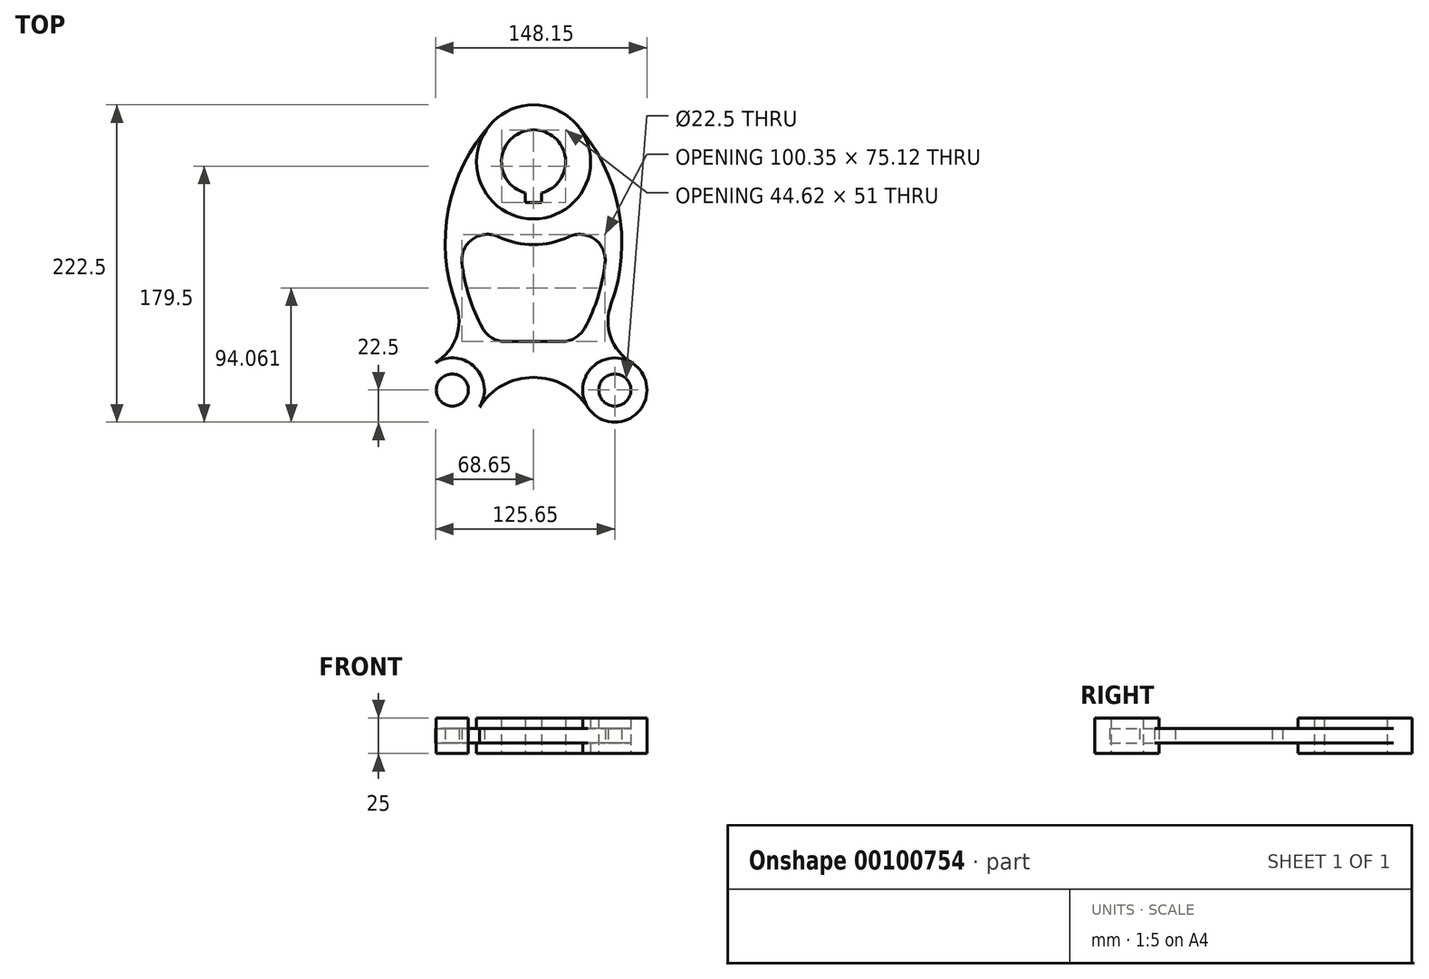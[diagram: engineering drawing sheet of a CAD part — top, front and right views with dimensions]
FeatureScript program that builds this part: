
annotation { "Feature Type Name" : "Feature", "Feature Type Description" : "" }
export const myFeature = defineFeature(function(context is Context, id is Id, definition is map)
    precondition{}
    {
        {
            var Q0;
            Q0=qCreatedBy(makeId("Top.planeOp"),FACE);
            var sketch = newSketch(context, id + "F0", { "sketchPlane" : qUnion([Q0])});
            skArc(sketch, "E0", {"start": v(5.75, -21.75) * mm, "mid": v(0, 22.5) * mm, "end": v(-5.75, -21.75) * mm});
            skCircle(sketch, "E1", {"center": v(0, 0) * mm, "radius": 40 * mm});
            skCircle(sketch, "E2", {"center": v(57, -160) * mm, "radius": 11.25 * mm});
            skCircle(sketch, "E3", {"center": v(57, -160) * mm, "radius": 22.5 * mm});
            skLineSegment(sketch, "E4", {"start": v(-5.75, -28.5) * mm, "end": v(5.75, -28.5) * mm});
            skLineSegment(sketch, "E5", {"start": v(-5.75, -28.5) * mm, "end": v(-5.75, -21.75) * mm});
            skLineSegment(sketch, "E6", {"start": v(5.75, -28.5) * mm, "end": v(5.75, -21.75) * mm});
            skLineSegment(sketch, "E7", {"start": v(0, -126) * mm, "end": v(20, -126) * mm});
            skArc(sketch, "E8", {"start": v(0, -58) * mm, "mid": v(12.62, -56.61) * mm, "end": v(24.64, -52.5) * mm});
            skArc(sketch, "E9", {"start": v(50.17, -70.79) * mm, "mid": v(42.76, -54.17) * mm, "end": v(24.64, -52.5) * mm});
            skArc(sketch, "E10", {"start": v(54.33, -99.97) * mm, "mid": v(59.65, -33.14) * mm, "end": v(29.67, 26.82) * mm});
            skLineSegment(sketch, "E11", {"start": v(0, 60.43) * mm, "end": v(0, -244.32) * mm, "construction": true});
            skArc(sketch, "E12", {"start": v(54.33, -99.97) * mm, "mid": v(54.17, -122.93) * mm, "end": v(68.65, -140.75) * mm});
            skArc(sketch, "E13", {"start": v(20, -126) * mm, "mid": v(29.2, -123.47) * mm, "end": v(35.82, -116.58) * mm});
            skArc(sketch, "E14.trimOffspring", {"start": v(35.82, -116.58) * mm, "mid": v(45.22, -94.38) * mm, "end": v(50.17, -70.79) * mm});
            skArc(sketch, "E15.MirrorCS", {"start": v(-35.82, -116.58) * mm, "mid": v(-45.22, -94.38) * mm, "end": v(-50.17, -70.79) * mm});
            skArc(sketch, "E16.MirrorCS", {"start": v(-54.33, -99.97) * mm, "mid": v(-59.65, -33.14) * mm, "end": v(-29.67, 26.82) * mm});
            skCircle(sketch, "E17.MirrorC", {"center": v(-57, -160) * mm, "radius": 22.5 * mm});
            skArc(sketch, "E18.MirrorCS", {"start": v(-54.33, -99.97) * mm, "mid": v(-54.17, -122.93) * mm, "end": v(-68.65, -140.75) * mm});
            skArc(sketch, "E19.MirrorCS", {"start": v(-20, -126) * mm, "mid": v(-29.2, -123.47) * mm, "end": v(-35.82, -116.58) * mm});
            skCircle(sketch, "E20.MirrorC", {"center": v(-57, -160) * mm, "radius": 11.25 * mm});
            skArc(sketch, "E21.MirrorCS", {"start": v(-50.17, -70.79) * mm, "mid": v(-42.76, -54.17) * mm, "end": v(-24.64, -52.5) * mm});
            skLineSegment(sketch, "E22.MirrorCS", {"start": v(0, -126) * mm, "end": v(-20, -126) * mm});
            skArc(sketch, "E23.MirrorCS", {"start": v(0, -58) * mm, "mid": v(-12.62, -56.61) * mm, "end": v(-24.64, -52.5) * mm});
            skArc(sketch, "E24", {"start": v(38, -172.05) * mm, "mid": v(0, -151.16) * mm, "end": v(-38, -172.05) * mm});
            skSolve(sketch);
        }
        {
            var Q0;
            Q0=makeQuery(id+"F0.imprint","IMPRINT",FACE,{"disambiguationData":[TD([[makeQuery(id+"F0.imprint","IMPRINT",EDGE,{"derivedFrom":sQuery(id+"F0.wireOp",EDGE,"E7")}),-1.0]])]});
            extrude(context, id + "F1", {"entities" : qUnion([Q0]), "endBound" : BoundingType.SYMMETRIC, "depth" : 10 * mm});
        }
        {
            var Q0;
            Q0=makeQuery(id+"F0.imprint","IMPRINT",FACE,{"disambiguationData":[TD([[makeQuery(id+"F0.imprint","IMPRINT",EDGE,{"derivedFrom":sQuery(id+"F0.wireOp",EDGE,"E20.MirrorC")}),1.0]])]});
            var Q1;
            Q1=makeQuery(id+"F0.imprint","IMPRINT",FACE,{"disambiguationData":[TD([[makeQuery(id+"F0.imprint","IMPRINT",EDGE,{"derivedFrom":sQuery(id+"F0.wireOp",EDGE,"E0")}),-1.0]])]});
            var Q2;
            Q2=makeQuery(id+"F0.imprint","IMPRINT",FACE,{"disambiguationData":[TD([[makeQuery(id+"F0.imprint","IMPRINT",EDGE,{"derivedFrom":sQuery(id+"F0.wireOp",EDGE,"E2")}),-1.0]])]});
            extrude(context, id + "F2", {"entities" : qUnion([Q0, Q1, Q2]), "operationType" : NewBodyOperationType.ADD, "endBound" : BoundingType.SYMMETRIC, "depth" : 25 * mm});
        }
    });
